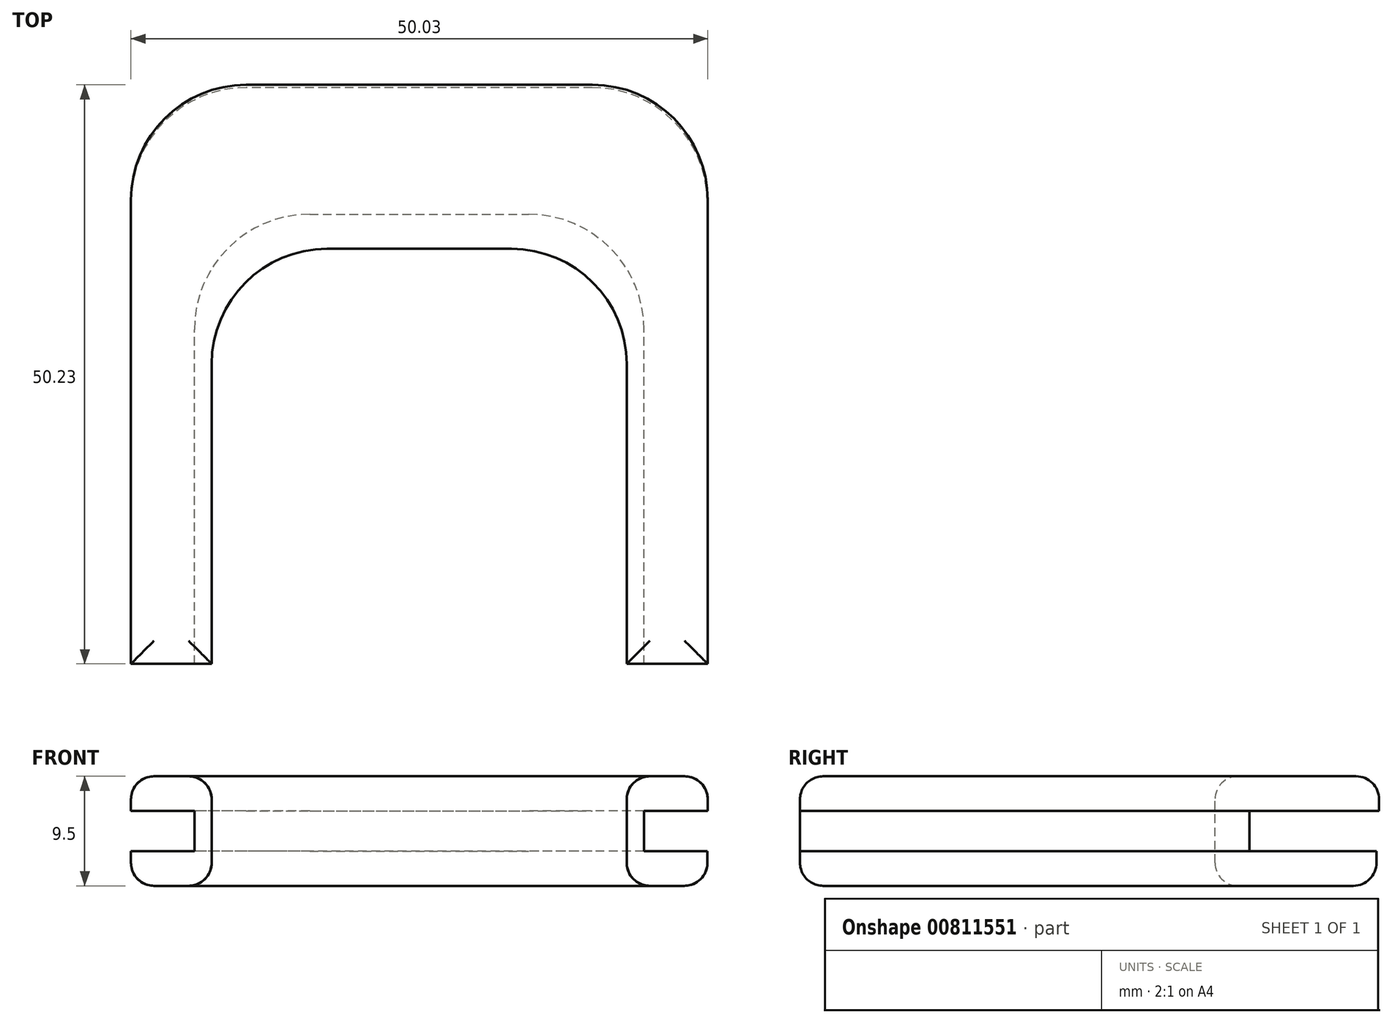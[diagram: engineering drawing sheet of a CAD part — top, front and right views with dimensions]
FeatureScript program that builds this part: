
annotation { "Feature Type Name" : "Feature", "Feature Type Description" : "" }
export const myFeature = defineFeature(function(context is Context, id is Id, definition is map)
    precondition{}
    {
        {
            var Q0;
            Q0=qCreatedBy(makeId("Top.planeOp"),FACE);
            var sketch = newSketch(context, id + "F0", { "sketchPlane" : qUnion([Q0])});
            skLineSegment(sketch, "E0.bottom", {"start": v(25, -25) * mm, "end": v(-25, -25) * mm});
            skLineSegment(sketch, "E0.top", {"start": v(25, 25) * mm, "end": v(-25, 25) * mm});
            skLineSegment(sketch, "E0.left", {"start": v(25, -25) * mm, "end": v(25, 25) * mm});
            skLineSegment(sketch, "E0.right", {"start": v(-25, -25) * mm, "end": v(-25, 25) * mm});
            skPoint(sketch, "E0.middle", {"position": v(0, 0) * mm});
            skPoint(sketch, "E1.visualSharp", {"position": v(-25, 25) * mm});
            skLineSegment(sketch, "E1.filletArc", {"start": v(-25, 25) * mm, "end": v(-25, 25) * mm});
            skPoint(sketch, "E2.visualSharp", {"position": v(25, 25) * mm});
            skLineSegment(sketch, "E2.filletArc", {"start": v(25, 25) * mm, "end": v(25, 25) * mm});
            skSolve(sketch);
        }
        {
            var Q0;
            Q0 = qSketchRegion(id + "F0", true);
            extrude(context, id + "F1", {"entities" : qUnion([Q0]), "depth" : 3 * mm, "offsetDistance" : 25 * mm});
        }
        {
            var Q0;
            Q0=makeQuery(id+"F1.opExtrude","CAP_FACE",FACE,{"disambiguationData":[OSD([sQuery(id+"F0.wireOp",EDGE,"E0.bottom"),sQuery(id+"F0.wireOp",EDGE,"E0.top"),sQuery(id+"F0.wireOp",EDGE,"E0.left"),sQuery(id+"F0.wireOp",EDGE,"E0.right"),sQuery(id+"F0.wireOp",EDGE,"E1.filletArc"),sQuery(id+"F0.wireOp",EDGE,"E2.filletArc")])],"isStart":false});
            var sketch = newSketch(context, id + "F2", { "sketchPlane" : qUnion([Q0])});
            skLineSegment(sketch, "E3.bottom", {"start": v(-19.5, -25) * mm, "end": v(19.5, -25) * mm});
            skLineSegment(sketch, "E3.top", {"start": v(-19.5, 14) * mm, "end": v(19.5, 14) * mm});
            skLineSegment(sketch, "E3.left", {"start": v(-19.5, -25) * mm, "end": v(-19.5, 14) * mm});
            skLineSegment(sketch, "E3.right", {"start": v(19.5, -25) * mm, "end": v(19.5, 14) * mm});
            skLineSegment(sketch, "E4", {"start": v(0, 25) * mm, "end": v(0, -25) * mm, "construction": true});
            skPoint(sketch, "E5.visualSharp", {"position": v(-19.5, 14) * mm});
            skLineSegment(sketch, "E5.filletArc", {"start": v(-19.5, 14) * mm, "end": v(-19.5, 14) * mm});
            skPoint(sketch, "E6.visualSharp", {"position": v(19.5, 14) * mm});
            skLineSegment(sketch, "E6.filletArc", {"start": v(19.5, 14) * mm, "end": v(19.5, 14) * mm});
            skSolve(sketch);
        }
        {
            var Q0;
            Q0 = qSketchRegion(id + "F2", true);
            extrude(context, id + "F3", {"entities" : qUnion([Q0]), "operationType" : NewBodyOperationType.ADD, "depth" : 3.5 * mm, "offsetDistance" : 25 * mm});
        }
        {
            var Q0;
            Q0=makeQuery(id+"F3.opExtrude","CAP_FACE",FACE,{"disambiguationData":[OSD([sQuery(id+"F2.wireOp",EDGE,"E3.bottom"),sQuery(id+"F2.wireOp",EDGE,"E3.top"),sQuery(id+"F2.wireOp",EDGE,"E3.left"),sQuery(id+"F2.wireOp",EDGE,"E3.right"),sQuery(id+"F2.wireOp",EDGE,"E5.filletArc"),sQuery(id+"F2.wireOp",EDGE,"E6.filletArc")])],"isStart":false});
            var sketch = newSketch(context, id + "F4", { "sketchPlane" : qUnion([Q0])});
            skLineSegment(sketch, "E7.bottom", {"start": v(-18, -25) * mm, "end": v(18, -25) * mm});
            skLineSegment(sketch, "E7.top", {"start": v(-18, 11) * mm, "end": v(18, 11) * mm});
            skLineSegment(sketch, "E7.left", {"start": v(-18, -25) * mm, "end": v(-18, 11) * mm});
            skLineSegment(sketch, "E7.right", {"start": v(18, -25) * mm, "end": v(18, 11) * mm});
            skLineSegment(sketch, "E8", {"start": v(0, 25.07) * mm, "end": v(0, -25) * mm});
            skPoint(sketch, "E9.visualSharp", {"position": v(-18, 11) * mm});
            skLineSegment(sketch, "E9.filletArc", {"start": v(-18, 11) * mm, "end": v(-18, 11) * mm});
            skPoint(sketch, "E10.visualSharp", {"position": v(18, 11) * mm});
            skLineSegment(sketch, "E10.filletArc", {"start": v(18, 11) * mm, "end": v(18, 11) * mm});
            skSolve(sketch);
        }
        {
            var Q0;
            Q0=makeQuery(id+"F3.opExtrude","CAP_FACE",FACE,{"disambiguationData":[OSD([sQuery(id+"F2.wireOp",EDGE,"E3.bottom"),sQuery(id+"F2.wireOp",EDGE,"E3.top"),sQuery(id+"F2.wireOp",EDGE,"E3.left"),sQuery(id+"F2.wireOp",EDGE,"E3.right"),sQuery(id+"F2.wireOp",EDGE,"E5.filletArc"),sQuery(id+"F2.wireOp",EDGE,"E6.filletArc")])],"isStart":false});
            var sketch = newSketch(context, id + "F5", { "sketchPlane" : qUnion([Q0])});
            skLineSegment(sketch, "E11.0", {"start": v(-19.5, -25) * mm, "end": v(-25, -25) * mm});
            skLineSegment(sketch, "E12.0", {"start": v(25, 25) * mm, "end": v(25, 25) * mm});
            skLineSegment(sketch, "E13.bottom", {"start": v(-25, -25) * mm, "end": v(25.03, -25) * mm});
            skLineSegment(sketch, "E13.top", {"start": v(-25, 25.23) * mm, "end": v(25.03, 25.23) * mm});
            skLineSegment(sketch, "E13.left", {"start": v(-25, -25) * mm, "end": v(-25, 25.23) * mm});
            skLineSegment(sketch, "E13.right", {"start": v(25.03, -25) * mm, "end": v(25.03, 25.23) * mm});
            skSolve(sketch);
        }
        {
            var Q0;
            Q0 = qSketchRegion(id + "F5", true);
            extrude(context, id + "F6", {"entities" : qUnion([Q0]), "operationType" : NewBodyOperationType.ADD, "depth" : 3 * mm, "offsetDistance" : 25 * mm});
        }
        {
            var Q0;
            Q0=makeQuery(id+"F1.opExtrude","SWEPT_EDGE",EDGE,{"disambiguationData":[OSD([sQuery(id+"F0.wireOp",EDGE,"E0.top"),sQuery(id+"F0.wireOp",EDGE,"E0.right")])]});
            var Q1;
            Q1=makeQuery(id+"F6.opExtrude","SWEPT_EDGE",EDGE,{"disambiguationData":[OSD([sQuery(id+"F5.wireOp",EDGE,"E13.top"),sQuery(id+"F5.wireOp",EDGE,"E13.left")])]});
            var Q2;
            Q2=makeQuery(id+"F6.opExtrude","SWEPT_EDGE",EDGE,{"disambiguationData":[OSD([sQuery(id+"F5.wireOp",EDGE,"E13.top"),sQuery(id+"F5.wireOp",EDGE,"E13.right")])]});
            var Q3;
            Q3=makeQuery(id+"F1.opExtrude","SWEPT_EDGE",EDGE,{"disambiguationData":[OSD([sQuery(id+"F0.wireOp",EDGE,"E0.top"),sQuery(id+"F0.wireOp",EDGE,"E0.left")])]});
            var Q4;
            Q4=makeQuery(id+"F3.opExtrude","SWEPT_EDGE",EDGE,{"disambiguationData":[OSD([sQuery(id+"F2.wireOp",EDGE,"E3.top"),sQuery(id+"F2.wireOp",EDGE,"E3.left")])]});
            var Q5;
            Q5=makeQuery(id+"F3.opExtrude","SWEPT_EDGE",EDGE,{"disambiguationData":[OSD([sQuery(id+"F2.wireOp",EDGE,"E3.top"),sQuery(id+"F2.wireOp",EDGE,"E3.right")])]});
            fillet(context, id + "F7", {"entities" : qUnion([Q0, Q1, Q2, Q3, Q4, Q5]), "radius" : 10 * mm, "tangentPropagation" : true, "allowEdgeOverflow" : false});
        }
        {
            var Q0;
            Q0=makeQuery(id+"F6.opExtrude","CAP_FACE",FACE,{"disambiguationData":[OSD([sQuery(id+"F5.wireOp",EDGE,"E13.bottom"),sQuery(id+"F5.wireOp",EDGE,"E13.top"),sQuery(id+"F5.wireOp",EDGE,"E13.left"),sQuery(id+"F5.wireOp",EDGE,"E13.right")])],"isStart":false});
            var sketch = newSketch(context, id + "F8", { "sketchPlane" : qUnion([Q0])});
            skLineSegment(sketch, "E14.bottom", {"start": v(-18, -25) * mm, "end": v(18, -25) * mm});
            skLineSegment(sketch, "E14.top", {"start": v(-8, 11) * mm, "end": v(8, 11) * mm});
            skLineSegment(sketch, "E14.left", {"start": v(-18, -25) * mm, "end": v(-18, 1) * mm});
            skLineSegment(sketch, "E14.right", {"start": v(18, -25) * mm, "end": v(18, 1) * mm});
            skLineSegment(sketch, "E15", {"start": v(0, 25.23) * mm, "end": v(0, -25) * mm, "construction": true});
            skPoint(sketch, "E16.visualSharp", {"position": v(-18, 11) * mm});
            skArc(sketch, "E16.filletArc", {"start": v(-8, 11) * mm, "mid": v(-15.07, 8.07) * mm, "end": v(-18, 1) * mm});
            skPoint(sketch, "E17.visualSharp", {"position": v(18, 11) * mm});
            skArc(sketch, "E17.filletArc", {"start": v(18, 1) * mm, "mid": v(15.07, 8.07) * mm, "end": v(8, 11) * mm});
            skSolve(sketch);
        }
        {
            var Q0;
            Q0 = qSketchRegion(id + "F8", true);
            var Q1;
            Q1=makeQuery(id+"F1.opExtrude","CAP_FACE",FACE,{"disambiguationData":[OSD([sQuery(id+"F0.wireOp",EDGE,"E0.bottom"),sQuery(id+"F0.wireOp",EDGE,"E0.top"),sQuery(id+"F0.wireOp",EDGE,"E0.left"),sQuery(id+"F0.wireOp",EDGE,"E0.right")])],"isStart":true});
            extrude(context, id + "F9", {"entities" : qUnion([Q0]), "operationType" : NewBodyOperationType.REMOVE, "endBound" : BoundingType.UP_TO_SURFACE, "oppositeDirection" : true, "depth" : 25 * mm, "endBoundEntityFace" : qUnion([Q1]), "offsetDistance" : 25 * mm});
        }
        {
            var Q0;
            Q0=makeQuery(id+"F6.opExtrude","CAP_FACE",FACE,{"disambiguationData":[OSD([sQuery(id+"F5.wireOp",EDGE,"E13.bottom"),sQuery(id+"F5.wireOp",EDGE,"E13.top"),sQuery(id+"F5.wireOp",EDGE,"E13.left"),sQuery(id+"F5.wireOp",EDGE,"E13.right")])],"isStart":false});
            var Q1;
            Q1=makeQuery(id+"F1.opExtrude","CAP_FACE",FACE,{"disambiguationData":[OSD([sQuery(id+"F0.wireOp",EDGE,"E0.bottom"),sQuery(id+"F0.wireOp",EDGE,"E0.top"),sQuery(id+"F0.wireOp",EDGE,"E0.left"),sQuery(id+"F0.wireOp",EDGE,"E0.right")])],"isStart":true});
            fillet(context, id + "F10", {"entities" : qUnion([Q0, Q1]), "radius" : 2 * mm, "tangentPropagation" : true, "allowEdgeOverflow" : false});
        }
    });
